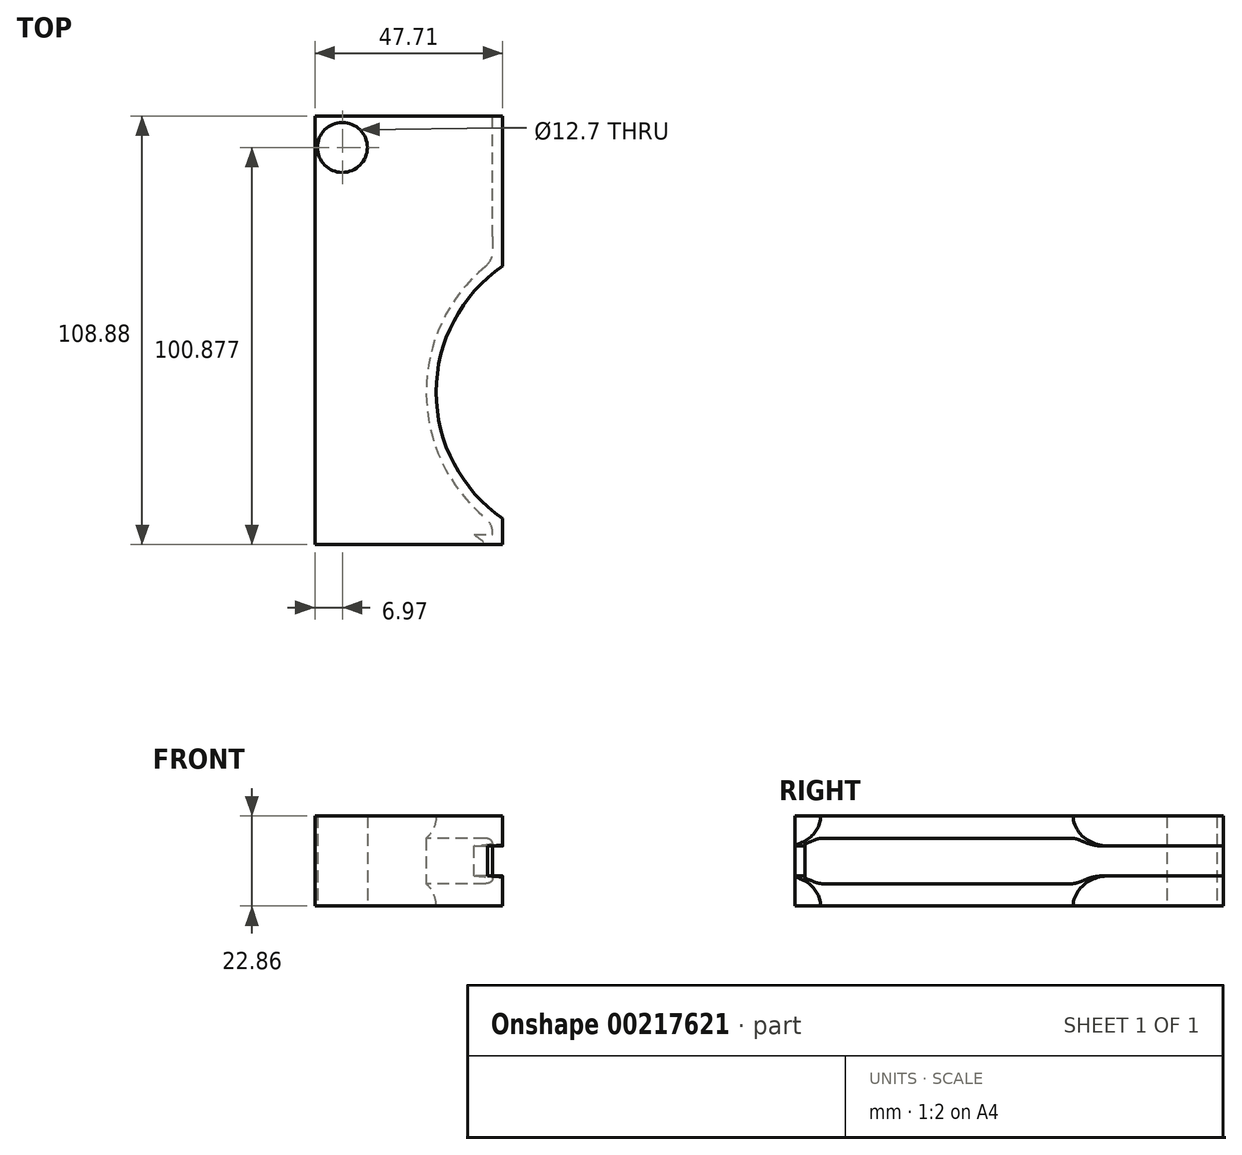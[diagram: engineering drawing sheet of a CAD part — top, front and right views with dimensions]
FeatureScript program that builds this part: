
annotation { "Feature Type Name" : "Feature", "Feature Type Description" : "" }
export const myFeature = defineFeature(function(context is Context, id is Id, definition is map)
    precondition{}
    {
        {
            var Q0;
            Q0=qCreatedBy(makeId("Top.planeOp"),FACE);
            var sketch = newSketch(context, id + "F0", { "sketchPlane" : qUnion([Q0])});
            skLineSegment(sketch, "E0.bottom", {"start": v(-54.46, -51.88) * mm, "end": v(-9.3, -51.88) * mm});
            skLineSegment(sketch, "E0.top", {"start": v(-54.46, 54.46) * mm, "end": v(-9.3, 54.46) * mm});
            skLineSegment(sketch, "E0.left", {"start": v(-54.46, -51.88) * mm, "end": v(-54.46, 54.46) * mm});
            skLineSegment(sketch, "E0.right", {"start": v(-9.3, -51.88) * mm, "end": v(-9.3, -49.13) * mm});
            skArc(sketch, "E1", {"start": v(-9.3, 17.64) * mm, "mid": v(-26.18, -15.74) * mm, "end": v(-9.3, -49.13) * mm});
            skLineSegment(sketch, "E2.trimOffspring", {"start": v(-9.3, 17.64) * mm, "end": v(-9.3, 54.46) * mm});
            skSolve(sketch);
        }
        {
            var Q0;
            Q0 = qSketchRegion(id + "F0", true);
            extrude(context, id + "F1", {"entities" : qUnion([Q0]), "depth" : 7.62 * mm});
        }
        {
            var Q0;
            Q0=makeQuery(id+"F1.opExtrude","CAP_FACE",FACE,{"disambiguationData":[OSD([sQuery(id+"F0.wireOp",EDGE,"E0.bottom"),sQuery(id+"F0.wireOp",EDGE,"E0.top"),sQuery(id+"F0.wireOp",EDGE,"E0.left"),sQuery(id+"F0.wireOp",EDGE,"E0.right"),sQuery(id+"F0.wireOp",EDGE,"E1"),sQuery(id+"F0.wireOp",EDGE,"E2.trimOffspring")])],"isStart":true});
            var sketch = newSketch(context, id + "F2", { "sketchPlane" : qUnion([Q0])});
            skLineSegment(sketch, "E3.0", {"start": v(-6.75, -16.33) * mm, "end": v(-6.75, -54.46) * mm});
            skArc(sketch, "E3.1", {"start": v(-6.75, -16.33) * mm, "mid": v(-23.64, 15.74) * mm, "end": v(-6.75, 47.82) * mm});
            skLineSegment(sketch, "E3.2", {"start": v(-6.75, 54.42) * mm, "end": v(-6.75, 47.82) * mm});
            skLineSegment(sketch, "E3.3", {"start": v(-54.46, 54.42) * mm, "end": v(-6.75, 54.42) * mm});
            skLineSegment(sketch, "E4", {"start": v(-6.75, -54.46) * mm, "end": v(-54.46, -54.46) * mm});
            skLineSegment(sketch, "E5", {"start": v(-54.46, -54.46) * mm, "end": v(-54.46, 54.42) * mm});
            skSolve(sketch);
        }
        {
            var Q0;
            Q0 = qSketchRegion(id + "F2", true);
            extrude(context, id + "F3", {"entities" : qUnion([Q0]), "operationType" : NewBodyOperationType.ADD, "depth" : 7.62 * mm});
        }
        {
            var Q0;
            Q0=makeQuery(id+"F1.opExtrude","CAP_FACE",FACE,{"disambiguationData":[OSD([sQuery(id+"F0.wireOp",EDGE,"E0.bottom"),sQuery(id+"F0.wireOp",EDGE,"E0.top"),sQuery(id+"F0.wireOp",EDGE,"E0.left"),sQuery(id+"F0.wireOp",EDGE,"E0.right"),sQuery(id+"F0.wireOp",EDGE,"E1"),sQuery(id+"F0.wireOp",EDGE,"E2.trimOffspring")])],"isStart":false});
            var sketch = newSketch(context, id + "F4", { "sketchPlane" : qUnion([Q0])});
            skLineSegment(sketch, "E6.0", {"start": v(-6.75, 16.33) * mm, "end": v(-6.75, 54.46) * mm});
            skArc(sketch, "E6.1", {"start": v(-6.75, 16.33) * mm, "mid": v(-23.64, -15.74) * mm, "end": v(-6.75, -47.82) * mm});
            skLineSegment(sketch, "E6.2", {"start": v(-6.75, -54.42) * mm, "end": v(-6.75, -47.82) * mm});
            skLineSegment(sketch, "E6.3", {"start": v(-54.46, -54.42) * mm, "end": v(-6.75, -54.42) * mm});
            skLineSegment(sketch, "E7", {"start": v(-54.46, -54.42) * mm, "end": v(-54.46, 54.46) * mm});
            skLineSegment(sketch, "E8", {"start": v(-54.46, 54.46) * mm, "end": v(-6.75, 54.46) * mm});
            skSolve(sketch);
        }
        {
            var Q0;
            Q0 = qSketchRegion(id + "F4", true);
            extrude(context, id + "F5", {"entities" : qUnion([Q0]), "operationType" : NewBodyOperationType.ADD, "depth" : 7.62 * mm});
        }
        {
            var Q0;
            Q0=makeQuery(id+"F3.opExtrude","CAP_FACE",FACE,{"disambiguationData":[OSD([sQuery(id+"F2.wireOp",EDGE,"E3.0"),sQuery(id+"F2.wireOp",EDGE,"E3.1"),sQuery(id+"F2.wireOp",EDGE,"E3.2"),sQuery(id+"F2.wireOp",EDGE,"E3.3"),sQuery(id+"F2.wireOp",EDGE,"E4"),sQuery(id+"F2.wireOp",EDGE,"E5")])],"isStart":false});
            var sketch = newSketch(context, id + "F6", { "sketchPlane" : qUnion([Q0])});
            skCircle(sketch, "E9", {"center": v(-47.49, -46.46) * mm, "radius": 5.7 * mm});
            skSolve(sketch);
        }
        {
            var Q0;
            Q0=sQuery(id+"F6.wireOp",VERTEX,"E9.center");
            var Q1;
            Q1=makeQuery(id+"F1.opExtrude","SWEPT_BODY",BODY,{"disambiguationData":[OSD([sQuery(id+"F0.wireOp",EDGE,"E0.bottom"),sQuery(id+"F0.wireOp",EDGE,"E0.top"),sQuery(id+"F0.wireOp",EDGE,"E0.left"),sQuery(id+"F0.wireOp",EDGE,"E0.right"),sQuery(id+"F0.wireOp",EDGE,"E1"),sQuery(id+"F0.wireOp",EDGE,"E2.trimOffspring")])]});
            hole(context, id + "F7", {"style" : HoleStyle.SIMPLE, "endStyle" : HoleEndStyle.THROUGH, "holeDiameter" : 12.7 * mm, "locations" : qUnion([Q0]), "scope" : qUnion([Q1]), "isTappedThrough" : true});
        }
        {
            var Q0;
            Q0=makeQuery(id+"F3.opExtrude","CAP_EDGE",EDGE,{"disambiguationData":[OSD([sQuery(id+"F2.wireOp",EDGE,"E3.1")])],"isStart":true});
            var Q1;
            Q1=makeQuery(id+"F5.opExtrude","CAP_EDGE",EDGE,{"disambiguationData":[OSD([sQuery(id+"F4.wireOp",EDGE,"E6.1")])],"isStart":true});
            fillet(context, id + "F8", {"entities" : qUnion([Q0, Q1]), "radius" : 7.62 * mm, "tangentPropagation" : true, "allowEdgeOverflow" : false});
        }
        {
            var Q0;
            Q0=makeQuery(id+"F1.opExtrude","SWEPT_EDGE",EDGE,{"disambiguationData":[OSD([sQuery(id+"F0.wireOp",EDGE,"E0.right"),sQuery(id+"F0.wireOp",EDGE,"E1")])]});
            fillet(context, id + "F9", {"entities" : qUnion([Q0]), "radius" : 5.08 * mm, "tangentPropagation" : true, "allowEdgeOverflow" : false});
        }
        {
            var Q0;
            Q0=makeQuery(id+"F1.opExtrude","SWEPT_EDGE",EDGE,{"disambiguationData":[OSD([sQuery(id+"F0.wireOp",EDGE,"E1"),sQuery(id+"F0.wireOp",EDGE,"E2.trimOffspring")])]});
            fillet(context, id + "F10", {"entities" : qUnion([Q0]), "radius" : 5.08 * mm, "tangentPropagation" : true, "allowEdgeOverflow" : false});
        }
        {
            var Q0;
            Q0=makeQuery(id+"F8.opFillet","SPLIT",FACE,{"disambiguationData":[OD(0.0)],"derivedFrom":makeQuery(id+"F5.opExtrude","CAP_FACE",FACE,{"disambiguationData":[OSD([sQuery(id+"F4.wireOp",EDGE,"E6.0"),sQuery(id+"F4.wireOp",EDGE,"E6.1"),sQuery(id+"F4.wireOp",EDGE,"E6.2"),sQuery(id+"F4.wireOp",EDGE,"E6.3"),sQuery(id+"F4.wireOp",EDGE,"E7"),sQuery(id+"F4.wireOp",EDGE,"E8")])],"isStart":true})});
            extrude(context, id + "F11", {"entities" : qUnion([Q0]), "operationType" : NewBodyOperationType.ADD, "depth" : 7.62 * mm});
        }
    });
